# Revit family: TD92_ZAP385_AZU070_RVT20_R00
name_source: partatom
category: Mobiliário
units: mm (PartAtom-declared; Revit-internal decimal feet)

## family parameters
Com base no plano de trabalho = Não
Compartilhado = Não
Corte com vazios quando carregada = Não
Número OmniClass = 23.40.20.00
Ponto de cálculo do ambiente = Não
Sempre na vertical = Sim
Título OmniClass = General Furniture and Specialties

## types (1)
- TD92_ZAP385_AZU070_RVT20_R00
    Descrição = Para deixar a vida das crianças ainda mais especiais, insira o Escorregador Infantil Tramontina Zap em Polietileno. Produzido em material livre de toxinas, ele é indicado para crianças de 1 a 3 anos e suporta até 30 kg de felicidade e diversão. Ele pode ser colocado em ambientes residenciais, como quartos e áreas de brinquedos, ou em ambientes comerciais, como playgrounds de condomínios ou restaurantes. Além disso, é de encaixar e pode ser utilizado com outros acessórios infantis da Tramontina!
    Elevação padrão = 0  [stored 0 ft]
    Fabricante = Tramontina Delta S/A
    Modelo = Escorregador Infantil Tramontina Zap em Polietileno Azul
    Nota-chave = 92385070
    URL = https://www.tramontinastore.com

note: [stored X ft] marks values corroborated as IEEE doubles in the binary element streams (Revit-internal decimal feet)
